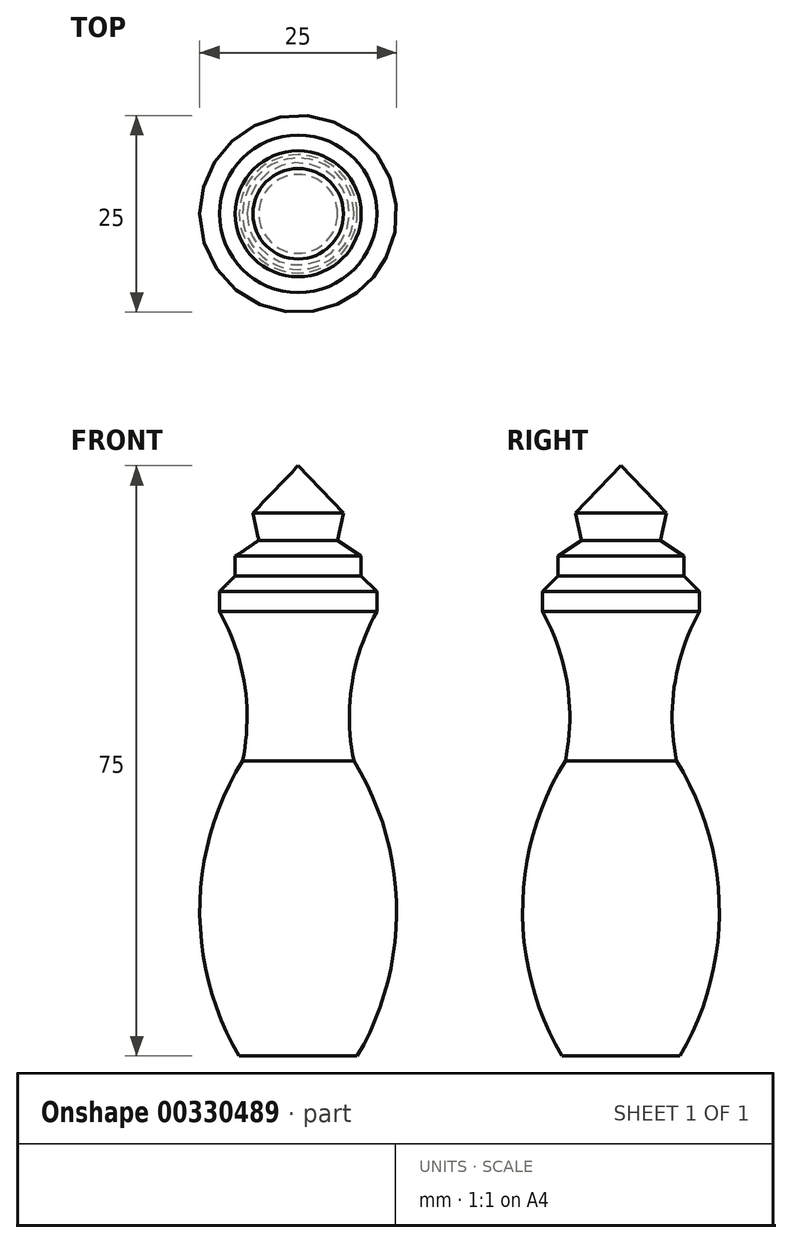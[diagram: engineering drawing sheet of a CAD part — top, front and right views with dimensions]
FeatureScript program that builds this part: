
annotation { "Feature Type Name" : "Feature", "Feature Type Description" : "" }
export const myFeature = defineFeature(function(context is Context, id is Id, definition is map)
    precondition{}
    {
        {
            var Q0;
            Q0=qCreatedBy(makeId("Front.planeOp"),FACE);
            var sketch = newSketch(context, id + "F0", { "sketchPlane" : qUnion([Q0])});
            skLineSegment(sketch, "E0", {"start": v(7.5, -75) * mm, "end": v(0, -75) * mm});
            skLineSegment(sketch, "E1", {"start": v(0, -75) * mm, "end": v(0, 0) * mm});
            skArc(sketch, "E2", {"start": v(7.5, -75) * mm, "mid": v(12.5, -56.2) * mm, "end": v(7.07, -37.5) * mm});
            skLineSegment(sketch, "E3", {"start": v(0, 0) * mm, "end": v(5.75, -6) * mm});
            skLineSegment(sketch, "E4", {"start": v(5.75, -6) * mm, "end": v(5, -9.5) * mm});
            skLineSegment(sketch, "E5", {"start": v(5, -9.5) * mm, "end": v(8, -11.5) * mm});
            skLineSegment(sketch, "E6", {"start": v(8, -11.5) * mm, "end": v(8, -14) * mm});
            skLineSegment(sketch, "E7", {"start": v(8, -14) * mm, "end": v(10, -16) * mm});
            skLineSegment(sketch, "E8", {"start": v(10, -16) * mm, "end": v(10, -18.5) * mm});
            skArc(sketch, "E9", {"start": v(10, -18.5) * mm, "mid": v(6.82, -27.74) * mm, "end": v(7.07, -37.5) * mm});
            skSolve(sketch);
        }
        {
            var Q0;
            Q0=makeQuery(id+"F0.imprint","IMPRINT",FACE,{"disambiguationData":[TD([[makeQuery(id+"F0.imprint","IMPRINT",EDGE,{"derivedFrom":sQuery(id+"F0.wireOp",EDGE,"E0")}),-1.0]])]});
            var Q1;
            Q1=sQuery(id+"F0.wireOp",EDGE,"E1");
            revolve(context, id + "F1", {"entities" : qUnion([Q0]), "axis" : qUnion([Q1]), "revolveType" : RevolveType.FULL});
        }
    });
